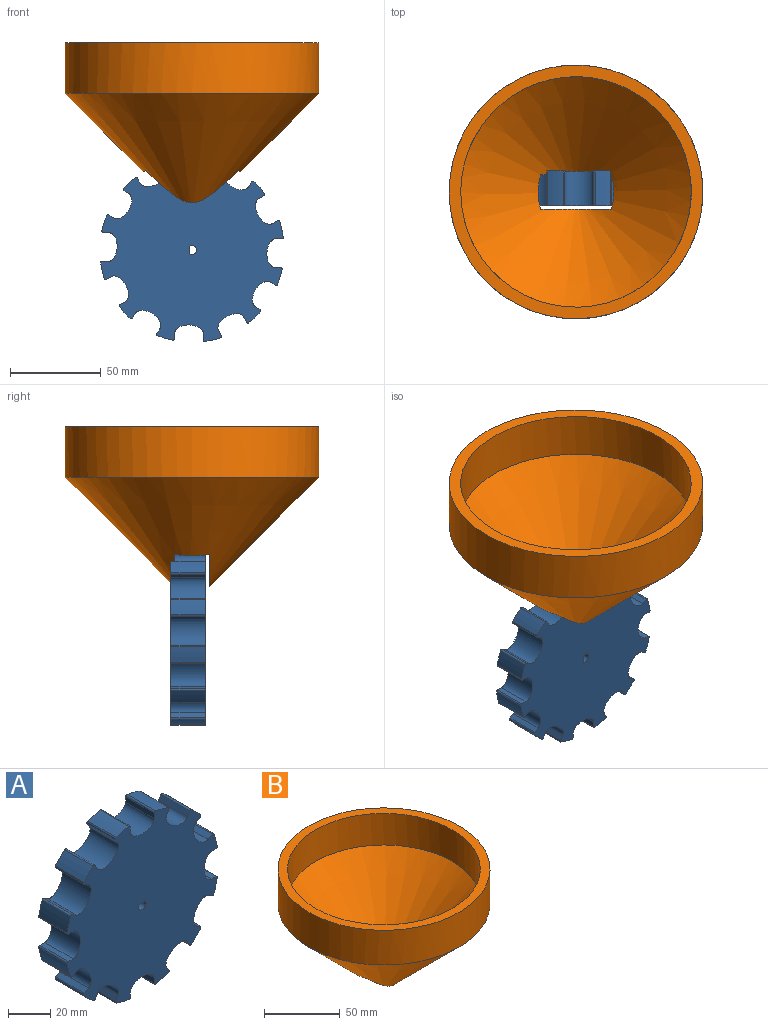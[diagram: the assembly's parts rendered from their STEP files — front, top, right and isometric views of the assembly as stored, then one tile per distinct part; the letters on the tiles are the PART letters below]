
ASSEMBLY  parts=2 mates=1
PART A: 76 faces, bbox 100.1x19.1x100.1 mm
  f0: plane 100.06x100.06mm, normal (0,-1,0), area 6505.4mm2, adj f2,f3,f4,f5,f6,f7,f8,f9
  f1: plane 100.06x100.06mm, normal (0,1,0), area 6505.4mm2, adj f2,f3,f4,f5,f6,f7,f8,f9
  f2: cylinder r=50.8mm len=19.05mm, axis (0,1,0), area 167mm2, adj f0,f1,f67,f73
  f3: cylinder r=50.8mm len=19.05mm, axis (0,1,0), area 167mm2, adj f0,f1,f62,f68
  f4: cylinder r=50.8mm len=19.05mm, axis (0,1,0), area 167mm2, adj f0,f1,f57,f63
  f5: cylinder r=50.8mm len=19.05mm, axis (0,1,0), area 167mm2, adj f0,f1,f52,f58
  f6: cylinder r=50.8mm len=19.05mm, axis (0,1,0), area 167mm2, adj f0,f1,f47,f53
  f7: cylinder r=50.8mm len=19.05mm, axis (0,1,0), area 167mm2, adj f0,f1,f42,f48
  f8: cylinder r=50.8mm len=19.05mm, axis (0,1,0), area 167mm2, adj f0,f1,f37,f43
  f9: cylinder r=50.8mm len=19.05mm, axis (0,1,0), area 167mm2, adj f0,f1,f32,f38
  f10: cylinder r=50.8mm len=19.05mm, axis (0,1,0), area 167mm2, adj f0,f1,f27,f33
  f11: cylinder r=50.8mm len=19.05mm, axis (0,1,0), area 167mm2, adj f0,f1,f22,f28
  f12: cylinder r=50.8mm len=19.05mm, axis (0,1,0), area 167mm2, adj f0,f1,f17,f23
  f13: cylinder r=50.8mm len=19.05mm, axis (0,1,0), area 167mm2, adj f0,f1,f18,f72
  f14: plane 19.05x3.2mm, normal (1,0,0), area 61mm2, adj f0,f1,f15,f18
  f15: extruded ~19.05x15.88mm, area 386mm2, adj f0,f1,f14,f16
  f16: plane 19.05x3.2mm, normal (-1,0,0), area 61mm2, adj f0,f1,f15,f17
  f17: cylinder r=0.79mm len=19.05mm, axis (0,1,0), area 26.4mm2, adj f0,f1,f12,f16
  f18: cylinder r=0.79mm len=19.05mm, axis (0,1,0), area 26.4mm2, adj f0,f1,f13,f14
  f19: plane 19.05x2.77mm, normal (0.87,0,-0.5), area 61mm2, adj f0,f1,f20,f23
  f20: extruded ~19.05x14.14mm, area 386mm2, adj f0,f1,f19,f21
  f21: plane 19.05x2.77mm, normal (-0.87,0,0.5), area 61mm2, adj f0,f1,f20,f22
  f22: cylinder r=0.79mm len=19.05mm, axis (0,1,0), area 26.4mm2, adj f0,f1,f11,f21
  f23: cylinder r=0.79mm len=19.05mm, axis (0,1,0), area 26.4mm2, adj f0,f1,f12,f19
  f24: plane 19.05x2.77mm, normal (0.5,0,-0.87), area 61mm2, adj f0,f1,f25,f28
  f25: extruded ~19.05x14.14mm, area 386mm2, adj f0,f1,f24,f26
  f26: plane 19.05x2.77mm, normal (-0.5,0,0.87), area 61mm2, adj f0,f1,f25,f27
  f27: cylinder r=0.79mm len=19.05mm, axis (0,1,0), area 26.4mm2, adj f0,f1,f10,f26
  f28: cylinder r=0.79mm len=19.05mm, axis (0,1,0), area 26.4mm2, adj f0,f1,f11,f24
  f29: plane 19.05x3.2mm, normal (0,0,-1), area 61mm2, adj f0,f1,f30,f33
  f30: extruded ~19.05x15.88mm, area 386mm2, adj f0,f1,f29,f31
  f31: plane 19.05x3.2mm, normal (0,0,1), area 61mm2, adj f0,f1,f30,f32
  f32: cylinder r=0.79mm len=19.05mm, axis (0,1,0), area 26.4mm2, adj f0,f1,f9,f31
  f33: cylinder r=0.79mm len=19.05mm, axis (0,1,0), area 26.4mm2, adj f0,f1,f10,f29
  f34: plane 19.05x2.77mm, normal (-0.5,0,-0.87), area 61mm2, adj f0,f1,f35,f38
  f35: extruded ~19.05x14.14mm, area 386mm2, adj f0,f1,f34,f36
  f36: plane 19.05x2.77mm, normal (0.5,0,0.87), area 61mm2, adj f0,f1,f35,f37
  f37: cylinder r=0.79mm len=19.05mm, axis (0,1,0), area 26.4mm2, adj f0,f1,f8,f36
  f38: cylinder r=0.79mm len=19.05mm, axis (0,1,0), area 26.4mm2, adj f0,f1,f9,f34
  f39: plane 19.05x2.77mm, normal (-0.87,0,-0.5), area 61mm2, adj f0,f1,f40,f43
  f40: extruded ~19.05x14.14mm, area 386mm2, adj f0,f1,f39,f41
  f41: plane 19.05x2.77mm, normal (0.87,0,0.5), area 61mm2, adj f0,f1,f40,f42
  f42: cylinder r=0.79mm len=19.05mm, axis (0,1,0), area 26.4mm2, adj f0,f1,f7,f41
  f43: cylinder r=0.79mm len=19.05mm, axis (0,1,0), area 26.4mm2, adj f0,f1,f8,f39
  f44: plane 19.05x3.2mm, normal (-1,0,0), area 61mm2, adj f0,f1,f45,f48
  f45: extruded ~19.05x15.88mm, area 386mm2, adj f0,f1,f44,f46
  f46: plane 19.05x3.2mm, normal (1,0,0), area 61mm2, adj f0,f1,f45,f47
  f47: cylinder r=0.79mm len=19.05mm, axis (0,1,0), area 26.4mm2, adj f0,f1,f6,f46
  f48: cylinder r=0.79mm len=19.05mm, axis (0,1,0), area 26.4mm2, adj f0,f1,f7,f44
  f49: plane 19.05x2.77mm, normal (-0.87,0,0.5), area 61mm2, adj f0,f1,f50,f53
  f50: extruded ~19.05x14.14mm, area 386mm2, adj f0,f1,f49,f51
  f51: plane 19.05x2.77mm, normal (0.87,0,-0.5), area 61mm2, adj f0,f1,f50,f52
  f52: cylinder r=0.79mm len=19.05mm, axis (0,1,0), area 26.4mm2, adj f0,f1,f5,f51
  f53: cylinder r=0.79mm len=19.05mm, axis (0,1,0), area 26.4mm2, adj f0,f1,f6,f49
  f54: plane 19.05x2.77mm, normal (-0.5,0,0.87), area 61mm2, adj f0,f1,f55,f58
  f55: extruded ~19.05x14.14mm, area 386mm2, adj f0,f1,f54,f56
  f56: plane 19.05x2.77mm, normal (0.5,0,-0.87), area 61mm2, adj f0,f1,f55,f57
  f57: cylinder r=0.79mm len=19.05mm, axis (0,1,0), area 26.4mm2, adj f0,f1,f4,f56
  f58: cylinder r=0.79mm len=19.05mm, axis (0,1,0), area 26.4mm2, adj f0,f1,f5,f54
  f59: plane 19.05x3.2mm, normal (0,0,1), area 61mm2, adj f0,f1,f60,f63
  f60: extruded ~19.05x15.88mm, area 386mm2, adj f0,f1,f59,f61
  f61: plane 19.05x3.2mm, normal (0,0,-1), area 61mm2, adj f0,f1,f60,f62
  f62: cylinder r=0.79mm len=19.05mm, axis (0,1,0), area 26.4mm2, adj f0,f1,f3,f61
  f63: cylinder r=0.79mm len=19.05mm, axis (0,1,0), area 26.4mm2, adj f0,f1,f4,f59
  f64: plane 19.05x2.77mm, normal (0.5,0,0.87), area 61mm2, adj f0,f1,f65,f68
  f65: extruded ~19.05x14.14mm, area 386mm2, adj f0,f1,f64,f66
  f66: plane 19.05x2.77mm, normal (-0.5,0,-0.87), area 61mm2, adj f0,f1,f65,f67
  f67: cylinder r=0.79mm len=19.05mm, axis (0,1,0), area 26.4mm2, adj f0,f1,f2,f66
  f68: cylinder r=0.79mm len=19.05mm, axis (0,1,0), area 26.4mm2, adj f0,f1,f3,f64
  f69: plane 19.05x2.77mm, normal (0.87,0,0.5), area 61mm2, adj f0,f1,f70,f73
  f70: extruded ~19.05x14.14mm, area 386mm2, adj f0,f1,f69,f71
  f71: plane 19.05x2.77mm, normal (-0.87,0,-0.5), area 61mm2, adj f0,f1,f70,f72
  f72: cylinder r=0.79mm len=19.05mm, axis (0,1,0), area 26.4mm2, adj f0,f1,f13,f71
  f73: cylinder r=0.79mm len=19.05mm, axis (0,1,0), area 26.4mm2, adj f0,f1,f2,f69
  f74: plane 19.05x4mm, normal (0,0,-1), area 76.2mm2, adj f0,f1,f75
  f75: cylinder r=2.5mm len=19.05mm, axis (0,-1,0), area 210.9mm2, adj f0,f1,f74
PART B: 9 faces, bbox 139.7x139.7x88.4 mm
  f0: cone r=67.99mm half-angle=45deg, axis (0,0,1), area 20251.2mm2, adj f2,f5,f6,f7,f8
  f1: cone r=63.5mm half-angle=45deg, axis (0,0,1), area 16816mm2, adj f4,f5,f6,f7,f8
  f2: cylinder r=69.85mm len=139.7mm, axis (0,0,-1), area 12301.9mm2, adj f0,f3
  f3: plane 139.7x139.7mm, normal (0,0,1), area 2660.2mm2, adj f2,f4
  f4: cylinder r=63.5mm len=127mm, axis (0,0,-1), area 10134.1mm2, adj f1,f3
  f5: cylinder r=50.8mm len=19.05mm, axis (0,-1,0), area 129.3mm2, adj f0,f1,f7,f8
  f6: cylinder r=50.8mm len=19.05mm, axis (0,-1,0), area 129.3mm2, adj f0,f1,f7,f8
  f7: plane 51.4x21.04mm, normal (0,-1,0), area 406mm2, adj f0,f1,f5,f6
  f8: plane 51.4x21.04mm, normal (0,1,0), area 406mm2, adj f0,f1,f5,f6
PLACE A rot(axis=(0,-1,0),88deg) t=(0,0,0)mm
PLACE B rot(axis=(0,1,0),0deg) t=(0,-2.12,25.4)mm
MATE cylindrical B.f5 <-> A.f2  axis (0,-1,0) through (0,-2.12,0)mm
